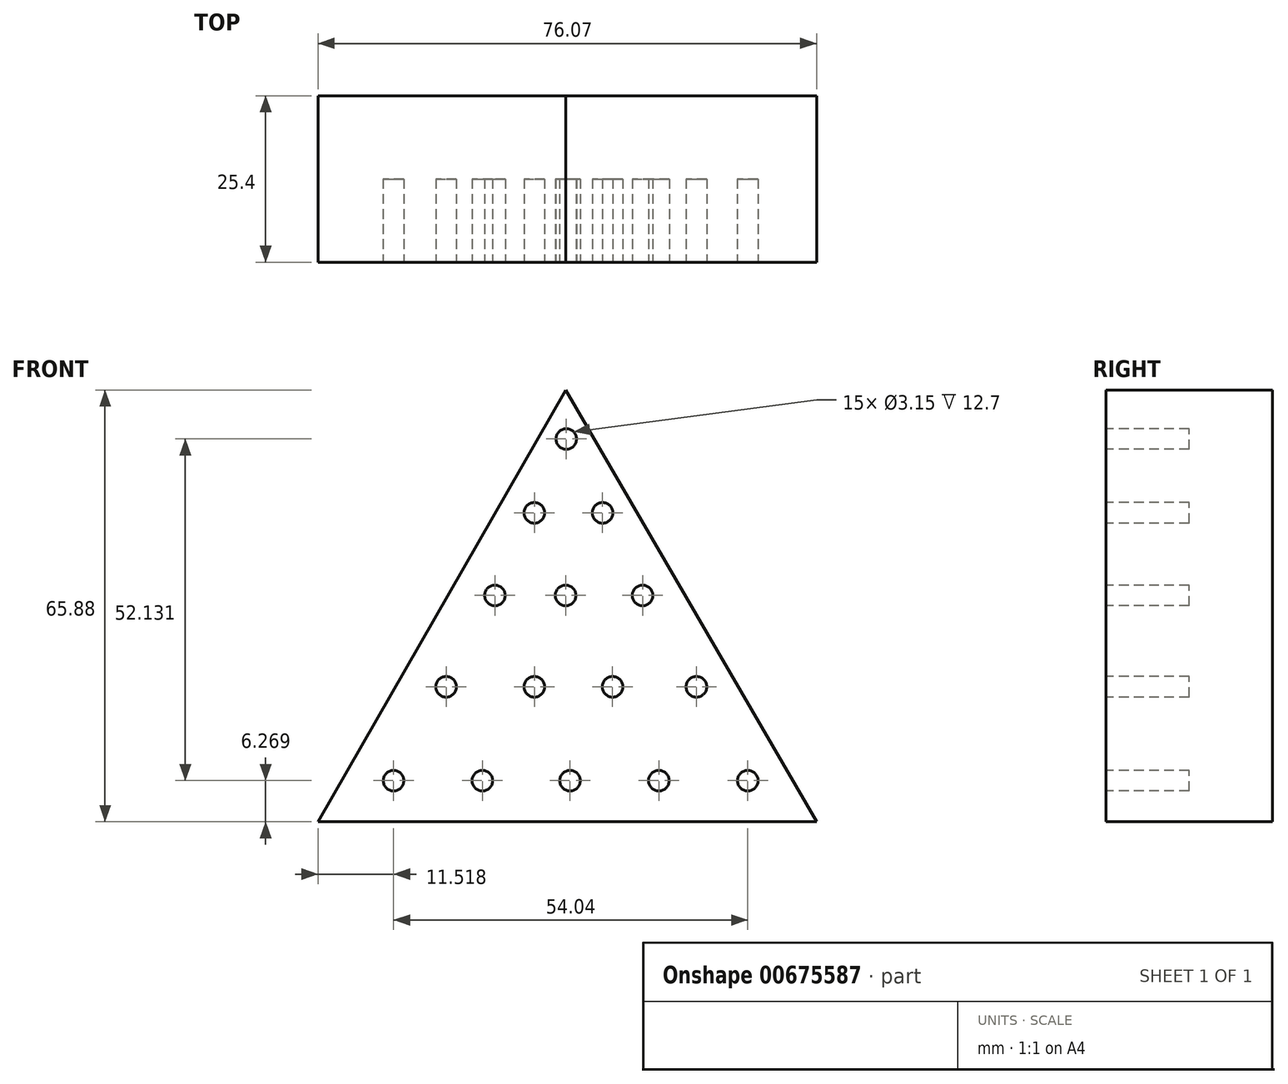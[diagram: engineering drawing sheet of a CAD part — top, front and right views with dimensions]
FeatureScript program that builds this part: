
annotation { "Feature Type Name" : "Feature", "Feature Type Description" : "" }
export const myFeature = defineFeature(function(context is Context, id is Id, definition is map)
    precondition{}
    {
        {
            var Q0;
            Q0=qCreatedBy(makeId("Front.planeOp"),FACE);
            var sketch = newSketch(context, id + "F0", { "sketchPlane" : qUnion([Q0])});
            skLineSegment(sketch, "E0", {"start": v(-33.13, -11.74) * mm, "end": v(4.78, 54.36) * mm});
            skLineSegment(sketch, "E1", {"start": v(4.78, 54.36) * mm, "end": v(43.07, -11.52) * mm});
            skLineSegment(sketch, "E2", {"start": v(43.07, -11.52) * mm, "end": v(-33.13, -11.52) * mm});
            skSolve(sketch);
        }
        {
            var Q0;
            Q0 = qSketchRegion(id + "F0", true);
            extrude(context, id + "F1", {"entities" : qUnion([Q0]), "depth" : 25.4 * mm, "offsetDistance" : 25.4 * mm});
        }
        {
            var Q0;
            Q0=makeQuery(id+"F1.opExtrude","CAP_FACE",FACE,{"disambiguationData":[OSD([sQuery(id+"F0.wireOp",EDGE,"E0"),sQuery(id+"F0.wireOp",EDGE,"E1"),sQuery(id+"F0.wireOp",EDGE,"E2")])],"isStart":false});
            var sketch = newSketch(context, id + "F2", { "sketchPlane" : qUnion([Q0])});
            skCircle(sketch, "E3", {"center": v(-21.48, -5.25) * mm, "radius": 1.57 * mm});
            skCircle(sketch, "E4", {"center": v(-7.92, -5.25) * mm, "radius": 1.57 * mm});
            skCircle(sketch, "E5", {"center": v(5.44, -5.25) * mm, "radius": 1.57 * mm});
            skCircle(sketch, "E6", {"center": v(19, -5.25) * mm, "radius": 1.57 * mm});
            skCircle(sketch, "E7", {"center": v(32.56, -5.25) * mm, "radius": 1.57 * mm});
            skSolve(sketch);
        }
        {
            var Q0;
            Q0 = qSketchRegion(id + "F2", true);
            extrude(context, id + "F3", {"entities" : qUnion([Q0]), "operationType" : NewBodyOperationType.REMOVE, "oppositeDirection" : true, "depth" : 12.7 * mm, "offsetDistance" : 25.4 * mm});
        }
        {
            var Q0;
            Q0=makeQuery(id+"F1.opExtrude","CAP_FACE",FACE,{"disambiguationData":[OSD([sQuery(id+"F0.wireOp",EDGE,"E0"),sQuery(id+"F0.wireOp",EDGE,"E1"),sQuery(id+"F0.wireOp",EDGE,"E2")])],"isStart":false});
            var sketch = newSketch(context, id + "F4", { "sketchPlane" : qUnion([Q0])});
            skCircle(sketch, "E8", {"center": v(-13.46, 9.07) * mm, "radius": 1.57 * mm});
            skCircle(sketch, "E9", {"center": v(0, 9.07) * mm, "radius": 1.57 * mm});
            skCircle(sketch, "E10", {"center": v(11.93, 9.07) * mm, "radius": 1.57 * mm});
            skCircle(sketch, "E11", {"center": v(24.73, 9.07) * mm, "radius": 1.57 * mm});
            skSolve(sketch);
        }
        {
            var Q0;
            Q0 = qSketchRegion(id + "F4", true);
            extrude(context, id + "F5", {"entities" : qUnion([Q0]), "operationType" : NewBodyOperationType.REMOVE, "oppositeDirection" : true, "depth" : 12.7 * mm, "offsetDistance" : 25.4 * mm});
        }
        {
            var Q0;
            Q0=makeQuery(id+"F1.opExtrude","CAP_FACE",FACE,{"disambiguationData":[OSD([sQuery(id+"F0.wireOp",EDGE,"E0"),sQuery(id+"F0.wireOp",EDGE,"E1"),sQuery(id+"F0.wireOp",EDGE,"E2")])],"isStart":false});
            var sketch = newSketch(context, id + "F6", { "sketchPlane" : qUnion([Q0])});
            skCircle(sketch, "E12", {"center": v(-6.02, 23.01) * mm, "radius": 1.57 * mm});
            skCircle(sketch, "E13", {"center": v(4.78, 23.01) * mm, "radius": 1.57 * mm});
            skCircle(sketch, "E14", {"center": v(16.52, 23.01) * mm, "radius": 1.57 * mm});
            skSolve(sketch);
        }
        {
            var Q0;
            Q0 = qSketchRegion(id + "F6", true);
            extrude(context, id + "F7", {"entities" : qUnion([Q0]), "operationType" : NewBodyOperationType.REMOVE, "oppositeDirection" : true, "depth" : 12.7 * mm, "offsetDistance" : 25.4 * mm});
        }
        {
            var Q0;
            Q0=makeQuery(id+"F1.opExtrude","CAP_FACE",FACE,{"disambiguationData":[OSD([sQuery(id+"F0.wireOp",EDGE,"E0"),sQuery(id+"F0.wireOp",EDGE,"E1"),sQuery(id+"F0.wireOp",EDGE,"E2")])],"isStart":false});
            var sketch = newSketch(context, id + "F8", { "sketchPlane" : qUnion([Q0])});
            skCircle(sketch, "E15", {"center": v(0, 35.61) * mm, "radius": 1.57 * mm});
            skCircle(sketch, "E16", {"center": v(10.4, 35.61) * mm, "radius": 1.57 * mm});
            skSolve(sketch);
        }
        {
            var Q0;
            Q0 = qSketchRegion(id + "F8", true);
            extrude(context, id + "F9", {"entities" : qUnion([Q0]), "operationType" : NewBodyOperationType.REMOVE, "oppositeDirection" : true, "depth" : 12.7 * mm, "offsetDistance" : 25.4 * mm});
        }
        {
            var Q0;
            Q0=makeQuery(id+"F1.opExtrude","CAP_FACE",FACE,{"disambiguationData":[OSD([sQuery(id+"F0.wireOp",EDGE,"E0"),sQuery(id+"F0.wireOp",EDGE,"E1"),sQuery(id+"F0.wireOp",EDGE,"E2")])],"isStart":false});
            var sketch = newSketch(context, id + "F10", { "sketchPlane" : qUnion([Q0])});
            skCircle(sketch, "E17", {"center": v(4.87, 46.88) * mm, "radius": 1.57 * mm});
            skSolve(sketch);
        }
        {
            var Q0;
            Q0 = qSketchRegion(id + "F10", true);
            extrude(context, id + "F11", {"entities" : qUnion([Q0]), "operationType" : NewBodyOperationType.REMOVE, "oppositeDirection" : true, "depth" : 12.7 * mm, "offsetDistance" : 25.4 * mm});
        }
    });
